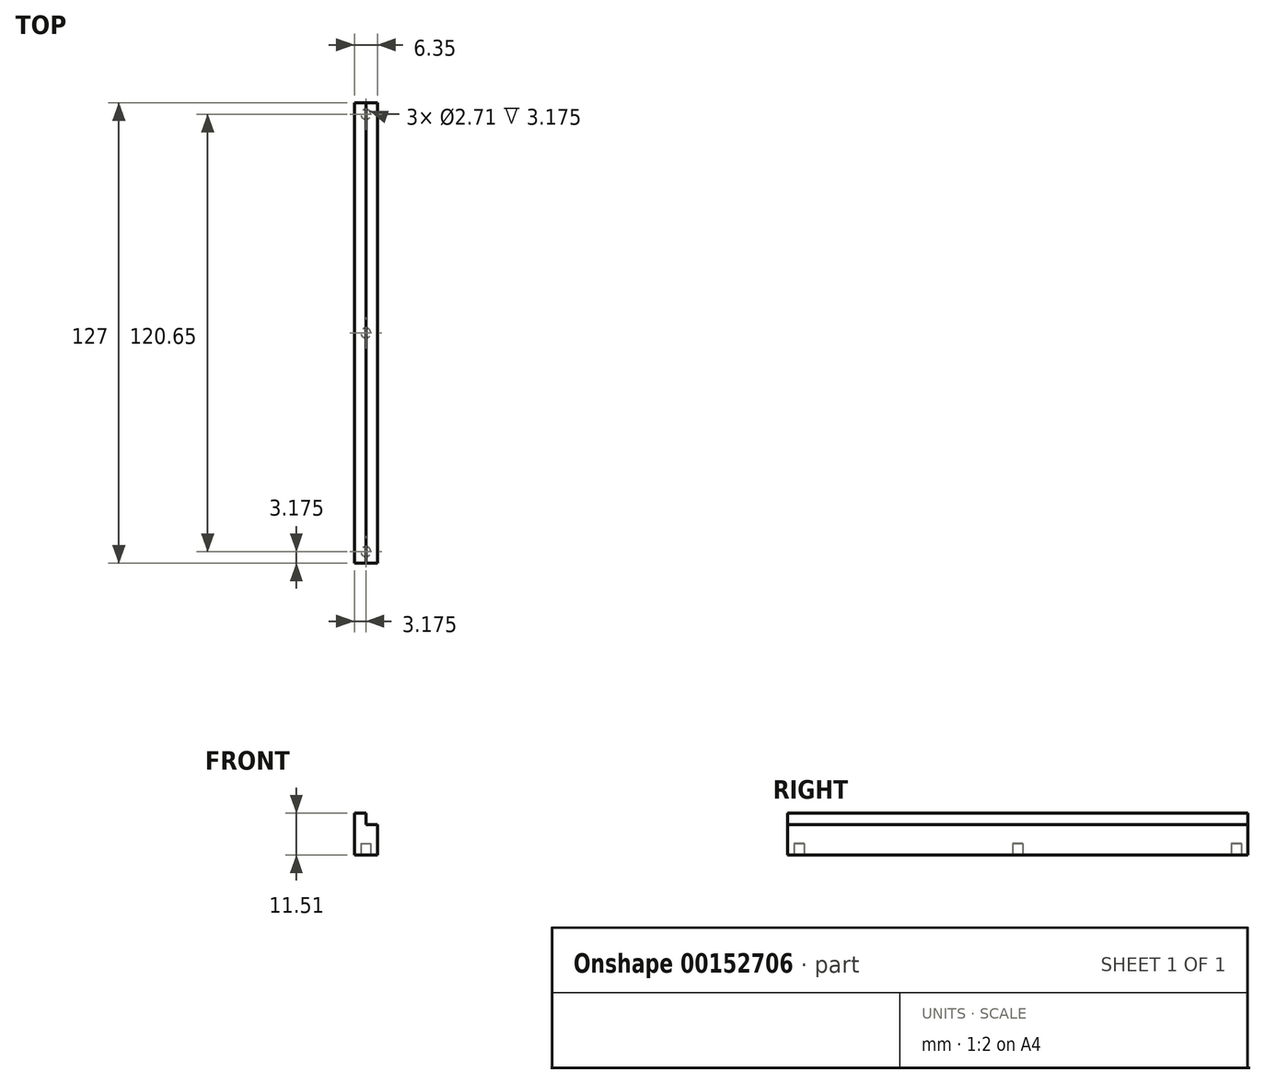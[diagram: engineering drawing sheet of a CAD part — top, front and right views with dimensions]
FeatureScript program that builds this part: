
annotation { "Feature Type Name" : "Feature", "Feature Type Description" : "" }
export const myFeature = defineFeature(function(context is Context, id is Id, definition is map)
    precondition{}
    {
        {
            var Q0;
            Q0=qCreatedBy(makeId("Top.planeOp"),FACE);
            var sketch = newSketch(context, id + "F0", { "sketchPlane" : qUnion([Q0])});
            skLineSegment(sketch, "E0.bottom", {"start": v(0, 0) * mm, "end": v(-6.35, 0) * mm});
            skLineSegment(sketch, "E0.top", {"start": v(0, -127) * mm, "end": v(-6.35, -127) * mm});
            skLineSegment(sketch, "E0.left", {"start": v(0, 0) * mm, "end": v(0, -127) * mm});
            skLineSegment(sketch, "E0.right", {"start": v(-6.35, 0) * mm, "end": v(-6.35, -127) * mm});
            skSolve(sketch);
        }
        {
            var Q0;
            Q0 = qSketchRegion(id + "F0", true);
            extrude(context, id + "F1", {"entities" : qUnion([Q0]), "depth" : 11.5 * mm});
        }
        {
            var Q0;
            Q0=makeQuery(id+"F1.opExtrude","SWEPT_FACE",FACE,{"disambiguationData":[OSD([sQuery(id+"F0.wireOp",EDGE,"E0.top")])]});
            var sketch = newSketch(context, id + "F2", { "sketchPlane" : qUnion([Q0])});
            skLineSegment(sketch, "E1.bottom", {"start": v(-3.18, 11.5) * mm, "end": v(0, 11.5) * mm});
            skLineSegment(sketch, "E1.top", {"start": v(-3.18, 8.33) * mm, "end": v(0, 8.33) * mm});
            skLineSegment(sketch, "E1.left", {"start": v(-3.18, 11.5) * mm, "end": v(-3.18, 8.33) * mm});
            skLineSegment(sketch, "E1.right", {"start": v(0, 11.5) * mm, "end": v(0, 8.33) * mm});
            skSolve(sketch);
        }
        {
            var Q0;
            Q0 = qSketchRegion(id + "F2", true);
            var Q1;
            Q1=makeQuery(id+"F1.opExtrude","SWEPT_FACE",FACE,{"disambiguationData":[OSD([sQuery(id+"F0.wireOp",EDGE,"E0.bottom")])]});
            extrude(context, id + "F3", {"entities" : qUnion([Q0]), "operationType" : NewBodyOperationType.REMOVE, "endBound" : BoundingType.UP_TO_SURFACE, "oppositeDirection" : true, "endBoundEntityFace" : qUnion([Q1]), "depth" : 25.4 * mm});
        }
        {
            var Q0;
            Q0=makeQuery(id+"F1.opExtrude","CAP_FACE",FACE,{"disambiguationData":[OSD([sQuery(id+"F0.wireOp",EDGE,"E0.bottom"),sQuery(id+"F0.wireOp",EDGE,"E0.top"),sQuery(id+"F0.wireOp",EDGE,"E0.left"),sQuery(id+"F0.wireOp",EDGE,"E0.right")])],"isStart":true});
            var sketch = newSketch(context, id + "F4", { "sketchPlane" : qUnion([Q0])});
            skLineSegment(sketch, "E2.bottom", {"start": v(-3.18, 127) * mm, "end": v(-6.35, 127) * mm, "construction": true});
            skLineSegment(sketch, "E2.top", {"start": v(-3.18, 123.83) * mm, "end": v(-6.35, 123.83) * mm, "construction": true});
            skLineSegment(sketch, "E2.left", {"start": v(-3.17, 127) * mm, "end": v(-3.17, 123.83) * mm, "construction": true});
            skLineSegment(sketch, "E2.right", {"start": v(-6.35, 127) * mm, "end": v(-6.35, 123.83) * mm, "construction": true});
            skLineSegment(sketch, "E3.bottom", {"start": v(-3.17, 0) * mm, "end": v(-6.35, 0) * mm, "construction": true});
            skLineSegment(sketch, "E3.top", {"start": v(-3.17, 3.17) * mm, "end": v(-6.35, 3.17) * mm, "construction": true});
            skLineSegment(sketch, "E3.left", {"start": v(-3.17, 0) * mm, "end": v(-3.17, 3.17) * mm, "construction": true});
            skLineSegment(sketch, "E3.right", {"start": v(-6.35, 0) * mm, "end": v(-6.35, 3.17) * mm, "construction": true});
            skLineSegment(sketch, "E4", {"start": v(-3.17, 123.83) * mm, "end": v(-3.17, 3.17) * mm, "construction": true});
            skCircle(sketch, "E5", {"center": v(-3.18, 123.83) * mm, "radius": 1.35 * mm});
            skCircle(sketch, "E6", {"center": v(-3.17, 63.5) * mm, "radius": 1.35 * mm});
            skCircle(sketch, "E7", {"center": v(-3.17, 3.17) * mm, "radius": 1.35 * mm});
            skSolve(sketch);
        }
        {
            var Q0;
            Q0 = qSketchRegion(id + "F4", true);
            extrude(context, id + "F5", {"entities" : qUnion([Q0]), "operationType" : NewBodyOperationType.REMOVE, "oppositeDirection" : true, "depth" : 3.17 * mm});
        }
    });
